# Revit family: QF_ELECTROLUXPROFESSIONAL_1LSNSR_TD6-16_E
name_source: partatom
category: Attrezzature speciali
units: mm (PartAtom-declared; Revit-internal decimal feet)

## family parameters
Basato su piano di lavoro = No
Condiviso = No
Punto di calcolo locali = No
Quota connettore circolare = Usa diametro
Sempre verticale = Sì
Taglio con vuoti quando caricato = No
Tipo di parte = Normale

## types (26) — shared parameters
Depth Actual = 1210 mm  [stored 3.96982 ft]
Height Actual = 1690 mm  [stored 5.54462 ft]
Latent Heat Output = 0.0
Length Actual = 715 mm  [stored 2.3458 ft]
Modello = TD6-16
Produttore = Electrolux Professional
Sensible Heat Output = 0.0
URL = www.electroluxprofessional.com
Weight = 189
zero-valued in all types: Gas KW, Prospetto di default

## per-type parameters (varying)
| type | Cycle | Descrizione | Item Number | Phase | Steam Pounds per Hour | Volts | Watts |
| 9872230051 | 60 Hz | TUMBLE DRYER TD6-16 MARINE 16KG/35LB GALVA.DRUM EL 18KW 480/60/3 COMPASS PRO 6G82 SLVR/SLVR DO.RIGHT REV STOP DISCON... | 1L0GDH | 3 | 0 | 480 V | 18800 W |
| 9872230019 | 60 Hz | TUMBLE DRYER TD6-16 MARINE 16KG/35LB GALVA.DRUM EL 18KW 440/60/3 COMPASS PRO 6G82 SLVR/SLVR DO.RIGHT REV DISCON DMPR | 1L0G4B | 3 | 0 | 440 V | 18800 W |
| 9872230009 | 50 Hz | TUMBLE DRYER TD6-16 16KG/35LB GALVA.DRUM EL 18KW 400/50/3N COMPASS PRO 6G82 SLVR/SLVR DO.RIGHT REV DISCON DMPR | 1L0G42 | 3 | 0 | 400 V | 18800 W |
| 9872230079 | 50 Hz | TUMBLE DRYER TD6-16 16KG/35LB SST DRUM EL 13,5KW 415/50/3N COMPASS PRO 6G82 SLVR/SLVR DO.RIGHT REV STOP DISCON DMPR | 1L0GZ8 | 3 | 0 | 415 V | 14300 W |
| 9872230046 | 50 Hz | TUMBLE DRYER TD6-16 16KG/35LB SST DRUM EL 18KW 400/50/3N COMPASS PRO 6G81 SLVR/SLVR DO.RIGHT REV MB STOP DISCON DMPR | 1LSPDK | 3 | 0 | 400 V | 18800 W |
| 9872230003 | 50 Hz | TUMBLE DRYER TD6-16 16KG/35LB GALVA.DRUM EL 18KW 400/50/3N COMPASS PRO 6G82 SLVR/SLVR DO.RIGHT REV STOP DISCON DMPR | 1L0G36 | 3 | 0 | 400 V | 18800 W |
| 9872230033 | 50 Hz | TUMBLE DRYER TD6-16 16KG/35LB GALVA.DRUM EL 13,5KW 400/50/3N COMPASS PRO 6A81 SLVR/SLVR DO.LEFT REV MB DISCON DMPR | 1L0G4N | 3 | 0 | 400 V | 14300 W |
| 9872230043 | 50 Hz | TUMBLE DRYER TD6-16 16KG/35LB SST DRUM EL 18KW 400/50/3 COMPASS PRO 6G81 SLVR/SLVR DO.RIGHT REV MB DISCON DMPR | 1L0GAS | 3 | 0 | 400 V | 18800 W |
| 9872230063 | 60 Hz | TUMBLE DRYER TD6-16 MARINE 16KG/35LB GALVA.DRUM EL 18KW 415/60/3N COMPASS PRO 6G82 SLVR/SLVR DO.LEFT REV STOP DISCON... | 1L0GN6 | 3 | 0 | 415 V | 18800 W |
| 9872230020 | 50 Hz | TUMBLE DRYER TD6-16 16KG/35LB SST DRUM EL 18KW 400/50/3N COMPASS PRO 6L80 2.I/O SLVR/SLVR DO.RIGHT EXT.PM. REV DISCO... | 1L0G4C | 3 | 0 | 400 V | 18800 W |
| 9872230018 | 50 Hz | TUMBLE DRYER TD6-16 16KG/35LB GALVA.DRUM EL 18KW 400/50/3 COMPASS PRO 6L80 2.I/O SLVR/SLVR DO.RIGHT EXT.PM. REV DISC... | 1L0G4A | 3 | 0 | 400 V | 18800 W |
| 9872230028 | 50 Hz | TUMBLE DRYER TD6-16 16KG/35LB SST DRUM EL 18KW 415/50/3N COMPASS PRO 6G81 SST/SST DO.RIGHT REV MB STOP DISCON DMPR | 1L0G4L | 3 | 0 | 415 V | 18800 W |
| 9872230058 | 50 Hz | TUMBLE DRYER TD6-16 16KG/35LB GALVA.DRUM EL 13,5KW 400/50/3N COMPASS PRO 6G82 SLVR/SLVR DO.RIGHT REV DISCON DMPR | 1LA221 | 3 | 0 | 400 V | 14300 W |
| 9872230078 | 50 Hz | TUMBLE DRYER TD6-16 MARINE 16KG/35LB SST DRUM EL 18KW 415/50/3 COMPASS PRO 6G81 SST/SST DO.RIGHT REV MB STOP DISCON ... | 1L0GZ7 | 3 | 0 | 415 V | 18800 W |
| 9872230015 | 50 Hz | TUMBLE DRYER TD6-16 16KG/35LB GALVA.DRUM EL 13,5KW 400/50/3N COMPASS PRO 6G81 SLVR/SLVR DO.RIGHT REV MB STOP DISCON ... | 1L0G47 | 3 | 0 | 400 V | 14300 W |
| 9872230005 | 50 Hz | TUMBLE DRYER TD6-16 16KG/35LB SST DRUM EL 18KW 400/50/3 COMPASS PRO 6G82 SLVR/SLVR DO.RIGHT REV DISCON DMPR | 1L0G38 | 3 | 0 | 400 V | 18800 W |
| 9872230092 | 50 Hz | TUMBLE DRYER TD6-16 16KG/35LB SST DRUM EL 18KW 400/50/3 COMPASS PRO 6G82 SLVR/SLVR DO.RIGHT REV DISCON DMPR | 1L0H5K | 3 | 0 | 400 V | 18800 W |
| 9872230104 | 50 Hz | TUMBLE DRYER TD6-16 16KG/35LB SST DRUM EL 18KW 400/50/3N COMPASS PRO 6L85 2.I/O SLVR/SLVR DO.LEFT EXT.PM. REV DISCON... | 1LT6GJ | 3 | 41 | 400 V | 18800 W |
| 9872230002 | 50 Hz | TUMBLE DRYER TD6-16 16KG/35LB SST DRUM EL 18KW 400/50/3 COMPASS PRO 6G81 SLVR/SLVR DO.RIGHT REV MB DISCON DMPR | 1L0G35 | 3 | 0 | 400 V | 18800 W |
| 9872230042 | 60 Hz | TUMBLE DRYER TD6-16 MARINE 16KG/35LB SST DRUM EL 13,5KW 230/60/1 COMPASS PRO 6G82 SLVR/SLVR DO.RIGHT REV DISCON DMPR | 1LSP8P | 1 | 0 | 230 V | 14300 W |
| 9872230017 | 50 Hz | TUMBLE DRYER TD6-16 16KG/35LB GALVA.DRUM EL 13,5KW 400/50/3N COMPASS PRO 6L80 SLVR/SLVR DO.RIGHT REV DISCON DMPR | 1L0G49 | 3 | 0 | 400 V | 14300 W |
| 9872230007 | 50 Hz | TUMBLE DRYER TD6-16 16KG/35LB GALVA.DRUM EL 18KW 400/50/3N COMPASS PRO 6L80 2.I/O SLVR/SLVR DO.RIGHT EXT.PM. REV DIS... | 1L0G41 | 3 | 0 | 400 V | 18800 W |
| 9872230027 | 50 Hz | TUMBLE DRYER TD6-16 16KG/35LB GALVA.DRUM EL 13,5KW 230/50/3 COMPASS PRO 6G81 SLVR/SLVR DO.RIGHT REV MB STOP DISCON DMPR | 1L0G4K | 3 | 0 | 230 V | 14300 W |
| 9872230067 | 50 Hz | TUMBLE DRYER TD6-16 16KG/35LB GALVA.DRUM EL 13,5KW 400/50/3N COMPASS PRO 6G81 SLVR/SLVR DO.LEFT REV MB STOP DISCON DMPR | 1LA25A | 3 | 0 | 400 V | 14300 W |
| 9872230014 | 50 Hz | TUMBLE DRYER TD6-16 16KG/35LB GALVA.DRUM EL 18KW 400/50/3N COMPASS PRO 6G81 SLVR/SLVR DO.RIGHT REV MB DISCON DMPR | 1L0G46 | 3 | 0 | 400 V | 18800 W |
| 9872230024 | 50 Hz | TUMBLE DRYER TD6-16 16KG/35LB GALVA.DRUM EL 18KW 415/50/3N COMPASS PRO 6G81 SLVR/SLVR DO.RIGHT REV MB DISCON DMPR | 1L0G4G | 3 | 0 | 415 V | 18800 W |

note: [stored X ft] marks values corroborated as IEEE doubles in the binary element streams (Revit-internal decimal feet)

## geometry (parser evidence)
native form markers: Blend x8
no freeform markers — native parametric forms only
